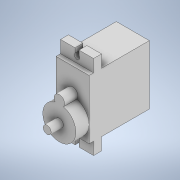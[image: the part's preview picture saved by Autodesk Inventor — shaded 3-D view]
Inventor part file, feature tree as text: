
AUTODESK INVENTOR PART (.ipt)
format: ipt  version: 2020 (Build 240168000, 168)  size: 175,616 bytes
history: native  units: mm
features: extrude x6, sketch x6, other x1
ambient origin geometry x8: Origin, YZ Plane, XZ Plane, XY Plane, X Axis, Y Axis, Z Axis, Center Point
bodies: Body1 (feature_tree)
feature tree (13):
  other  "Твердое тело1"
  extrude  "Выдавливание1"  Depth=12.5mm
  extrude  "Выдавливание2"  Depth=22.4mm
  extrude  "Выдавливание3"  Depth=22.8mm TaperAngle=0.0deg
  extrude  "Выдавливание4"  Depth=18.1mm
  extrude  "Выдавливание5"  Depth=3.0mm
  extrude  "Выдавливание6"  Depth=4.7mm TaperAngle=0.0deg
  sketch  "Эскиз2"
  sketch  "Эскиз3"
  sketch  "Эскиз4"
  sketch  "Эскиз5"
  sketch  "Эскиз6"
  sketch  "Эскиз7"
